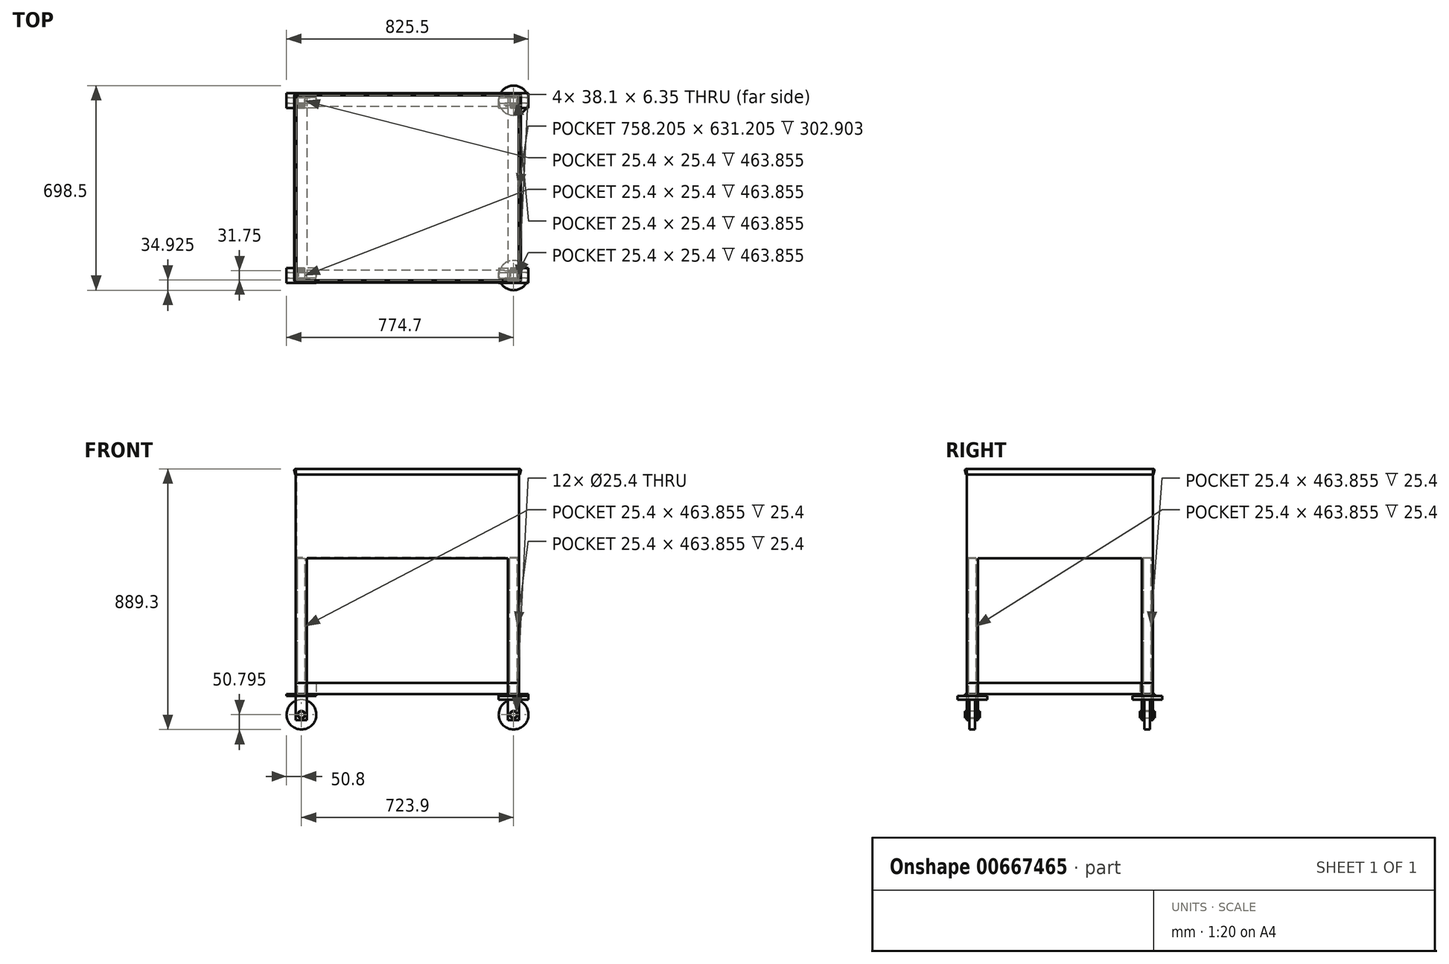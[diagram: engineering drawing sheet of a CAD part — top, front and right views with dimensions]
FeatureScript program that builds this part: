
annotation { "Feature Type Name" : "Feature", "Feature Type Description" : "" }
export const myFeature = defineFeature(function(context is Context, id is Id, definition is map)
    precondition{}
    {
        {
            var Q0;
            Q0=qCreatedBy(makeId("Top.planeOp"),FACE);
            var sketch = newSketch(context, id + "F0", { "sketchPlane" : qUnion([Q0])});
            skLineSegment(sketch, "E0.bottom", {"start": v(381, -317.5) * mm, "end": v(-381, -317.5) * mm});
            skLineSegment(sketch, "E0.top", {"start": v(381, 317.5) * mm, "end": v(-381, 317.5) * mm});
            skLineSegment(sketch, "E0.left", {"start": v(381, -317.5) * mm, "end": v(381, 317.5) * mm});
            skLineSegment(sketch, "E0.right", {"start": v(-381, -317.5) * mm, "end": v(-381, 317.5) * mm});
            skPoint(sketch, "E0.middle", {"position": v(0, 0) * mm});
            skSolve(sketch);
        }
        {
            var Q0;
            Q0=makeQuery(id+"F0.imprint","IMPRINT",FACE,{"disambiguationData":[TD([[makeQuery(id+"F0.imprint","IMPRINT",EDGE,{"derivedFrom":sQuery(id+"F0.wireOp",EDGE,"E0.bottom")}),-1.0]])]});
            extrude(context, id + "F1", {"entities" : qUnion([Q0]), "depth" : 304.8 * mm, "offsetDistance" : 25.4 * mm});
        }
        {
            var Q0;
            Q0=makeQuery(id+"F1.opExtrude","CAP_FACE",FACE,{"disambiguationData":[OSD([sQuery(id+"F0.wireOp",EDGE,"E0.bottom"),sQuery(id+"F0.wireOp",EDGE,"E0.top"),sQuery(id+"F0.wireOp",EDGE,"E0.left"),sQuery(id+"F0.wireOp",EDGE,"E0.right")])],"isStart":false});
            shell(context, id + "F2", {"entities" : qUnion([Q0]), "thickness" : 1.9 * mm});
        }
        {
            var Q0;
            Q0=makeQuery(id+"F1.opExtrude","CAP_FACE",FACE,{"disambiguationData":[OSD([sQuery(id+"F0.wireOp",EDGE,"E0.bottom"),sQuery(id+"F0.wireOp",EDGE,"E0.top"),sQuery(id+"F0.wireOp",EDGE,"E0.left"),sQuery(id+"F0.wireOp",EDGE,"E0.right")])],"isStart":true});
            var sketch = newSketch(context, id + "F3", { "sketchPlane" : qUnion([Q0])});
            skLineSegment(sketch, "E1.bottom", {"start": v(-381, 317.5) * mm, "end": v(-342.9, 317.5) * mm});
            skLineSegment(sketch, "E1.top", {"start": v(-381, 279.4) * mm, "end": v(-342.9, 279.4) * mm});
            skLineSegment(sketch, "E1.left", {"start": v(-381, 317.5) * mm, "end": v(-381, 279.4) * mm});
            skLineSegment(sketch, "E1.right", {"start": v(-342.9, 317.5) * mm, "end": v(-342.9, 279.4) * mm});
            skLineSegment(sketch, "E2.0", {"start": v(-374.65, 285.75) * mm, "end": v(-349.25, 285.75) * mm});
            skLineSegment(sketch, "E2.1", {"start": v(-374.65, 311.15) * mm, "end": v(-374.65, 285.75) * mm});
            skLineSegment(sketch, "E2.2", {"start": v(-374.65, 311.15) * mm, "end": v(-349.25, 311.15) * mm});
            skLineSegment(sketch, "E2.3", {"start": v(-349.25, 311.15) * mm, "end": v(-349.25, 285.75) * mm});
            skSolve(sketch);
        }
        {
            var Q0;
            Q0=makeQuery(id+"F3.imprint","IMPRINT",FACE,{"disambiguationData":[TD([[makeQuery(id+"F3.imprint","IMPRINT",EDGE,{"derivedFrom":sQuery(id+"F3.wireOp",EDGE,"E1.bottom")}),1.0]])]});
            extrude(context, id + "F4", {"entities" : qUnion([Q0]), "depth" : 457.2 * mm + 6.65 * mm, "offsetDistance" : 25.4 * mm});
        }
        {
            var Q0;
            Q0=makeQuery(id+"F4.opExtrude","CAP_FACE",FACE,{"disambiguationData":[OSD([sQuery(id+"F3.wireOp",EDGE,"E1.bottom"),sQuery(id+"F3.wireOp",EDGE,"E1.top"),sQuery(id+"F3.wireOp",EDGE,"E1.left"),sQuery(id+"F3.wireOp",EDGE,"E1.right"),sQuery(id+"F3.wireOp",EDGE,"E2.0"),sQuery(id+"F3.wireOp",EDGE,"E2.1"),sQuery(id+"F3.wireOp",EDGE,"E2.2"),sQuery(id+"F3.wireOp",EDGE,"E2.3")])],"isStart":false});
            var sketch = newSketch(context, id + "F5", { "sketchPlane" : qUnion([Q0])});
            skLineSegment(sketch, "E3.bottom", {"start": v(-311.15, 273.05) * mm, "end": v(-412.75, 273.05) * mm});
            skLineSegment(sketch, "E3.top", {"start": v(-311.15, 323.85) * mm, "end": v(-412.75, 323.85) * mm});
            skLineSegment(sketch, "E3.left", {"start": v(-311.15, 273.05) * mm, "end": v(-311.15, 323.85) * mm});
            skLineSegment(sketch, "E3.right", {"start": v(-412.75, 273.05) * mm, "end": v(-412.75, 323.85) * mm});
            skPoint(sketch, "E3.middle", {"position": v(-361.95, 298.45) * mm});
            skPoint(sketch, "E3.middle.positionSnap0", {"position": v(-374.65, 298.45) * mm});
            skPoint(sketch, "E3.middle.positionSnap1", {"position": v(-361.95, 311.15) * mm});
            skPoint(sketch, "E3.centerSnap0", {"position": v(-374.65, 298.45) * mm});
            skPoint(sketch, "E3.centerSnap1", {"position": v(-361.95, 311.15) * mm});
            skSolve(sketch);
        }
        {
            var Q0;
            Q0=makeQuery(id+"F5.imprint","IMPRINT",FACE,{"disambiguationData":[TD([[makeQuery(id+"F5.imprint","IMPRINT",EDGE,{"derivedFrom":sQuery(id+"F5.wireOp",EDGE,"E3.bottom")}),-1.0]])]});
            var Q1;
            Q1=makeQuery(id+"F5.imprint","IMPRINT",FACE,{"disambiguationData":[TD([[makeQuery(id+"F5.imprint","IMPRINT",EDGE,{"derivedFrom":makeQuery(id+"F4.opExtrude","CAP_EDGE",EDGE,{"disambiguationData":[OSD([sQuery(id+"F3.wireOp",EDGE,"E1.bottom")])],"isStart":false})}),1.0]])]});
            var Q2;
            Q2=makeQuery(id+"F5.imprint","IMPRINT",FACE,{"disambiguationData":[TD([[makeQuery(id+"F5.imprint","IMPRINT",EDGE,{"derivedFrom":makeQuery(id+"F4.opExtrude","CAP_EDGE",EDGE,{"disambiguationData":[OSD([sQuery(id+"F3.wireOp",EDGE,"E2.0")])],"isStart":false})}),1.0]])]});
            extrude(context, id + "F6", {"entities" : qUnion([Q0, Q1, Q2]), "depth" : 6.35 * mm, "offsetDistance" : 25.4 * mm});
        }
        {
            var Q0;
            Q0=makeQuery(id+"F4.opExtrude","SWEPT_FACE",FACE,{"disambiguationData":[OSD([sQuery(id+"F3.wireOp",EDGE,"E1.bottom")])]});
            var sketch = newSketch(context, id + "F7", { "sketchPlane" : qUnion([Q0])});
            skLineSegment(sketch, "E4", {"start": v(-381, -463.85) * mm, "end": v(-381, -552.75) * mm});
            skLineSegment(sketch, "E5", {"start": v(-381, -552.75) * mm, "end": v(-342.9, -552.75) * mm});
            skLineSegment(sketch, "E6", {"start": v(-342.9, -552.75) * mm, "end": v(-342.9, -463.85) * mm});
            skCircle(sketch, "E7", {"center": v(-361.95, -533.7) * mm, "radius": 12.7 * mm});
            skSolve(sketch);
        }
        {
            var Q0;
            Q0=makeQuery(id+"F7.imprint","IMPRINT",FACE,{"disambiguationData":[TD([[makeQuery(id+"F7.imprint","IMPRINT",EDGE,{"derivedFrom":sQuery(id+"F7.wireOp",EDGE,"E4")}),1.0]])]});
            extrude(context, id + "F8", {"entities" : qUnion([Q0]), "depth" : -6.35 * mm, "offsetDistance" : 25.4 * mm});
        }
        {
            var Q0;
            Q0=makeQuery(id+"F6.opExtrude","SWEPT_FACE",FACE,{"disambiguationData":[OSD([sQuery(id+"F5.wireOp",EDGE,"E3.bottom")])]});
            var Q1;
            Q1=makeQuery(id+"F6.opExtrude","SWEPT_FACE",FACE,{"disambiguationData":[OSD([sQuery(id+"F5.wireOp",EDGE,"E3.top")])]});
            cPlane(context, id + "F9", {"entities" : qUnion([Q0, Q1]), "cplaneType" : CPlaneType.MID_PLANE, "offset" : 25.4 * mm, "width" : 152.4 * mm, "height" : 152.4 * mm});
        }
        {
            var Q0;
            Q0=makeQuery(id+"F8.opExtrude","SWEPT_BODY",BODY,{"disambiguationData":[OSD([sQuery(id+"F3.wireOp",EDGE,"E1.bottom"),sQuery(id+"F7.wireOp",EDGE,"E4"),sQuery(id+"F7.wireOp",EDGE,"E5"),sQuery(id+"F7.wireOp",EDGE,"E6"),sQuery(id+"F7.wireOp",EDGE,"E7")])]});
            var Q1;
            Q1=qCreatedBy(id+"F9.planeOp",FACE);
            mirror(context, id + "F10", {"operationType" : NewBodyOperationType.ADD, "entities" : qUnion([Q0]), "mirrorPlane" : qUnion([Q1])});
        }
        {
            var Q0;
            Q0=qCreatedBy(id+"F9.planeOp",FACE);
            var sketch = newSketch(context, id + "F11", { "sketchPlane" : qUnion([Q0])});
            skCircle(sketch, "E8", {"center": v(361.95, -533.7) * mm, "radius": 50.8 * mm});
            skCircle(sketch, "E9", {"center": v(361.95, -533.7) * mm, "radius": 12.7 * mm});
            skSolve(sketch);
        }
        {
            var Q0;
            Q0=makeQuery(id+"F11.imprint","IMPRINT",FACE,{"disambiguationData":[TD([[makeQuery(id+"F11.imprint","IMPRINT",EDGE,{"derivedFrom":sQuery(id+"F11.wireOp",EDGE,"E8")}),1.0]])]});
            extrude(context, id + "F12", {"entities" : qUnion([Q0]), "oppositeDirection" : true, "depth" : 19.05 * mm, "offsetDistance" : 25.4 * mm, "symmetric" : true});
        }
        {
            var Q0;
            Q0=qCreatedBy(id+"F9.planeOp",FACE);
            var sketch = newSketch(context, id + "F13", { "sketchPlane" : qUnion([Q0])});
            skCircle(sketch, "E10", {"center": v(361.95, -533.7) * mm, "radius": 11.11 * mm});
            skSolve(sketch);
        }
        {
            var Q0;
            Q0=makeQuery(id+"F13.imprint","IMPRINT",FACE,{"disambiguationData":[TD([[makeQuery(id+"F13.imprint","IMPRINT",EDGE,{"derivedFrom":sQuery(id+"F13.wireOp",EDGE,"E10")}),1.0]])]});
            extrude(context, id + "F14", {"entities" : qUnion([Q0]), "depth" : 50.8 * mm, "offsetDistance" : 25.4 * mm, "symmetric" : true});
        }
        {
            var Q0;
            Q0=makeQuery(id+"F12.opExtrude","SWEPT_BODY",BODY,{"disambiguationData":[OSD([sQuery(id+"F11.wireOp",EDGE,"E8"),sQuery(id+"F11.wireOp",EDGE,"E9")])]});
            var Q1;
            Q1=makeQuery(id+"F10.opPattern","COPY",BODY,{"derivedFrom":makeQuery(id+"F8.opExtrude","SWEPT_BODY",BODY,{"disambiguationData":[OSD([sQuery(id+"F3.wireOp",EDGE,"E1.bottom"),sQuery(id+"F7.wireOp",EDGE,"E4"),sQuery(id+"F7.wireOp",EDGE,"E5"),sQuery(id+"F7.wireOp",EDGE,"E6"),sQuery(id+"F7.wireOp",EDGE,"E7")])]}),"instanceName":"1"});
            var Q2;
            Q2=makeQuery(id+"F8.opExtrude","SWEPT_BODY",BODY,{"disambiguationData":[OSD([sQuery(id+"F3.wireOp",EDGE,"E1.bottom"),sQuery(id+"F7.wireOp",EDGE,"E4"),sQuery(id+"F7.wireOp",EDGE,"E5"),sQuery(id+"F7.wireOp",EDGE,"E6"),sQuery(id+"F7.wireOp",EDGE,"E7")])]});
            var Q3;
            Q3=makeQuery(id+"F4.opExtrude","SWEPT_BODY",BODY,{"disambiguationData":[OSD([sQuery(id+"F3.wireOp",EDGE,"E1.bottom"),sQuery(id+"F3.wireOp",EDGE,"E1.top"),sQuery(id+"F3.wireOp",EDGE,"E1.left"),sQuery(id+"F3.wireOp",EDGE,"E1.right"),sQuery(id+"F3.wireOp",EDGE,"E2.0"),sQuery(id+"F3.wireOp",EDGE,"E2.1"),sQuery(id+"F3.wireOp",EDGE,"E2.2"),sQuery(id+"F3.wireOp",EDGE,"E2.3")])]});
            var Q4;
            Q4=makeQuery(id+"F6.opExtrude","SWEPT_BODY",BODY,{"disambiguationData":[OSD([sQuery(id+"F5.wireOp",EDGE,"E3.bottom"),sQuery(id+"F5.wireOp",EDGE,"E3.top"),sQuery(id+"F5.wireOp",EDGE,"E3.left"),sQuery(id+"F5.wireOp",EDGE,"E3.right")])]});
            var Q5;
            Q5=makeQuery(id+"F14.opExtrude","SWEPT_BODY",BODY,{"disambiguationData":[OSD([sQuery(id+"F13.wireOp",EDGE,"E10")])]});
            var Q6;
            Q6=qCreatedBy(makeId("Front.planeOp"),FACE);
            mirror(context, id + "F15", {"operationType" : NewBodyOperationType.ADD, "entities" : qUnion([Q0, Q1, Q2, Q3, Q4, Q5]), "mirrorPlane" : qUnion([Q6])});
        }
        {
            var Q0;
            Q0=makeQuery(id+"F12.opExtrude","SWEPT_BODY",BODY,{"disambiguationData":[OSD([sQuery(id+"F11.wireOp",EDGE,"E8"),sQuery(id+"F11.wireOp",EDGE,"E9")])]});
            var Q1;
            Q1=makeQuery(id+"F1.opExtrude","SWEPT_BODY",BODY,{"disambiguationData":[OSD([sQuery(id+"F0.wireOp",EDGE,"E0.bottom"),sQuery(id+"F0.wireOp",EDGE,"E0.top"),sQuery(id+"F0.wireOp",EDGE,"E0.left"),sQuery(id+"F0.wireOp",EDGE,"E0.right")])]});
            var Q2;
            Q2=makeQuery(id+"F14.opExtrude","SWEPT_BODY",BODY,{"disambiguationData":[OSD([sQuery(id+"F13.wireOp",EDGE,"E10")])]});
            var Q3;
            Q3=makeQuery(id+"F15.opPattern","COPY",BODY,{"derivedFrom":makeQuery(id+"F12.opExtrude","SWEPT_BODY",BODY,{"disambiguationData":[OSD([sQuery(id+"F11.wireOp",EDGE,"E8"),sQuery(id+"F11.wireOp",EDGE,"E9")])]}),"instanceName":"1"});
            var Q4;
            Q4=makeQuery(id+"F15.opPattern","COPY",BODY,{"derivedFrom":makeQuery(id+"F14.opExtrude","SWEPT_BODY",BODY,{"disambiguationData":[OSD([sQuery(id+"F13.wireOp",EDGE,"E10")])]}),"instanceName":"1"});
            var Q5;
            Q5=qCreatedBy(makeId("Right.planeOp"),FACE);
            mirror(context, id + "F16", {"operationType" : NewBodyOperationType.ADD, "entities" : qUnion([Q0, Q1, Q2, Q3, Q4]), "mirrorPlane" : qUnion([Q5])});
        }
        {
            var Q0;
            Q0=makeQuery(id+"F16.opPattern","COPY",FACE,{"derivedFrom":makeQuery(id+"F15.opPattern","COPY",FACE,{"derivedFrom":makeQuery(id+"F6.opExtrude","CAP_FACE",FACE,{"disambiguationData":[OSD([sQuery(id+"F5.wireOp",EDGE,"E3.bottom"),sQuery(id+"F5.wireOp",EDGE,"E3.top"),sQuery(id+"F5.wireOp",EDGE,"E3.left"),sQuery(id+"F5.wireOp",EDGE,"E3.right")])],"isStart":false}),"instanceName":"1"}),"instanceName":"1"});
            var sketch = newSketch(context, id + "F17", { "sketchPlane" : qUnion([Q0])});
            skCircle(sketch, "E11", {"center": v(361.95, -298.45) * mm, "radius": 50.8 * mm});
            skPoint(sketch, "E11.centerSnap0", {"position": v(412.75, -298.45) * mm});
            skLineSegment(sketch, "E12", {"start": v(361.95, -273.05) * mm, "end": v(361.95, -323.85) * mm});
            skSolve(sketch);
        }
        {
            var Q0;
            {var subQ0=sQuery(id+"F17.wireOp",EDGE,"E11");var subQ1=makeQuery(id+"F16.opPattern","COPY",EDGE,{"derivedFrom":makeQuery(id+"F15.opPattern","COPY",EDGE,{"derivedFrom":makeQuery(id+"F6.opExtrude","CAP_EDGE",EDGE,{"disambiguationData":[OSD([sQuery(id+"F5.wireOp",EDGE,"E3.bottom")])],"isStart":false}),"instanceName":"1"}),"instanceName":"1"});var subQ2=makeQuery(id+"F17.imprint","INTERSECT",VERTEX,{"disambiguationData":[OD(0.0)],"derivedFrom":[subQ1,subQ0]});Q0=makeQuery(id+"F17.imprint","IMPRINT",FACE,{"disambiguationData":[TD([[makeQuery(id+"F17.imprint","IMPRINT",EDGE,{"disambiguationData":[TD([[subQ2,1.0]])],"derivedFrom":subQ0}),1.0]])]});}
            var Q1;
            {var subQ7=sQuery(id+"F5.wireOp",EDGE,"E3.bottom");var subQ20=sQuery(id+"F17.wireOp",EDGE,"E11");var subQ21=makeQuery(id+"F16.opPattern","COPY",EDGE,{"derivedFrom":makeQuery(id+"F15.opPattern","COPY",EDGE,{"derivedFrom":makeQuery(id+"F6.opExtrude","CAP_EDGE",EDGE,{"disambiguationData":[OSD([subQ7])],"isStart":false}),"instanceName":"1"}),"instanceName":"1"});var subQ22=makeQuery(id+"F17.imprint","INTERSECT",VERTEX,{"disambiguationData":[OD(1.0)],"derivedFrom":[subQ21,subQ20]});Q1=makeQuery(id+"F17.imprint","IMPRINT",FACE,{"disambiguationData":[TD([[makeQuery(id+"F17.imprint","IMPRINT",EDGE,{"disambiguationData":[TD([[subQ22,1.0]])],"derivedFrom":subQ20}),1.0]])]});}
            var Q2;
            {var subQ3=sQuery(id+"F5.wireOp",EDGE,"E3.bottom");var subQ14=sQuery(id+"F17.wireOp",EDGE,"E11");var subQ15=makeQuery(id+"F16.opPattern","COPY",EDGE,{"derivedFrom":makeQuery(id+"F15.opPattern","COPY",EDGE,{"derivedFrom":makeQuery(id+"F6.opExtrude","CAP_EDGE",EDGE,{"disambiguationData":[OSD([subQ3])],"isStart":false}),"instanceName":"1"}),"instanceName":"1"});var subQ16=makeQuery(id+"F17.imprint","INTERSECT",VERTEX,{"disambiguationData":[OD(0.0)],"derivedFrom":[subQ15,subQ14]});Q2=makeQuery(id+"F17.imprint","IMPRINT",FACE,{"disambiguationData":[TD([[makeQuery(id+"F17.imprint","IMPRINT",EDGE,{"disambiguationData":[TD([[subQ16,-1.0]])],"derivedFrom":subQ14}),1.0]])]});}
            var Q3;
            {var subQ0=sQuery(id+"F17.wireOp",EDGE,"E11");var subQ1=makeQuery(id+"F16.opPattern","COPY",EDGE,{"derivedFrom":makeQuery(id+"F15.opPattern","COPY",EDGE,{"derivedFrom":makeQuery(id+"F6.opExtrude","CAP_EDGE",EDGE,{"disambiguationData":[OSD([sQuery(id+"F5.wireOp",EDGE,"E3.top")])],"isStart":false}),"instanceName":"1"}),"instanceName":"1"});var subQ2=makeQuery(id+"F17.imprint","INTERSECT",VERTEX,{"disambiguationData":[OD(0.0)],"derivedFrom":[subQ1,subQ0]});Q3=makeQuery(id+"F17.imprint","IMPRINT",FACE,{"disambiguationData":[TD([[makeQuery(id+"F17.imprint","IMPRINT",EDGE,{"disambiguationData":[TD([[subQ2,-1.0]])],"derivedFrom":subQ0}),1.0]])]});}
            var Q4;
            {var subQ4=sQuery(id+"F5.wireOp",EDGE,"E3.bottom");var subQ15=sQuery(id+"F17.wireOp",EDGE,"E11");var subQ23=makeQuery(id+"F16.opPattern","COPY",EDGE,{"derivedFrom":makeQuery(id+"F15.opPattern","COPY",EDGE,{"derivedFrom":makeQuery(id+"F6.opExtrude","CAP_EDGE",EDGE,{"disambiguationData":[OSD([subQ4])],"isStart":false}),"instanceName":"1"}),"instanceName":"1"});var subQ24=makeQuery(id+"F17.imprint","INTERSECT",VERTEX,{"disambiguationData":[OD(1.0)],"derivedFrom":[subQ23,subQ15]});Q4=makeQuery(id+"F17.imprint","IMPRINT",FACE,{"disambiguationData":[TD([[makeQuery(id+"F17.imprint","IMPRINT",EDGE,{"disambiguationData":[TD([[subQ24,-1.0]])],"derivedFrom":subQ15}),1.0]])]});}
            var Q5;
            Q5=sQuery(id+"F17.wireOp",EDGE,"E11");
            extrude(context, id + "F18", {"entities" : qUnion([Q0, Q1, Q2, Q3, Q4]), "surfaceEntities" : qUnion([Q5]), "depth" : 12.7 * mm, "offsetDistance" : 25.4 * mm});
        }
        {
            var Q0;
            Q0=makeQuery(id+"F18.opExtrude","SWEPT_BODY",BODY,{"disambiguationData":[OSD([sQuery(id+"F3.wireOp",EDGE,"E1.bottom"),sQuery(id+"F5.wireOp",EDGE,"E3.bottom"),sQuery(id+"F5.wireOp",EDGE,"E3.top"),sQuery(id+"F5.wireOp",EDGE,"E3.left"),sQuery(id+"F5.wireOp",EDGE,"E3.right"),sQuery(id+"F7.wireOp",EDGE,"E4"),sQuery(id+"F7.wireOp",EDGE,"E5"),sQuery(id+"F7.wireOp",EDGE,"E6"),sQuery(id+"F7.wireOp",EDGE,"E7"),sQuery(id+"F17.wireOp",EDGE,"E11")])]});
            var Q1;
            Q1=qCreatedBy(makeId("Front.planeOp"),FACE);
            mirror(context, id + "F19", {"entities" : qUnion([Q0]), "mirrorPlane" : qUnion([Q1])});
        }
        {
            var Q0;
            {var subQ0=makeQuery(id+"F4.opExtrude","SWEPT_FACE",FACE,{"disambiguationData":[OSD([sQuery(id+"F3.wireOp",EDGE,"E1.left")])]});Q0=makeQuery(id+"F15.boolean.opBoolean","MERGE",FACE,{"derivedFrom":[makeQuery(id+"F1.opExtrude","SWEPT_FACE",FACE,{"disambiguationData":[OSD([sQuery(id+"F0.wireOp",EDGE,"E0.right")])]}),subQ0,makeQuery(id+"F15.opPattern","COPY",FACE,{"derivedFrom":subQ0,"instanceName":"1"})]});}
            var sketch = newSketch(context, id + "F20", { "sketchPlane" : qUnion([Q0])});
            skLineSegment(sketch, "E13", {"start": v(-317.5, 304.8) * mm, "end": v(-319.05, 304.8) * mm});
            skLineSegment(sketch, "E14", {"start": v(-322.75, 300.13) * mm, "end": v(-319.35, 285.75) * mm});
            skLineSegment(sketch, "E15.0", {"start": v(-320.9, 300.57) * mm, "end": v(-317.5, 286.19) * mm});
            skLineSegment(sketch, "E15.1", {"start": v(-317.5, 302.9) * mm, "end": v(-319.05, 302.9) * mm});
            skLineSegment(sketch, "E16", {"start": v(-317.5, 286.19) * mm, "end": v(-319.35, 285.75) * mm});
            skPoint(sketch, "E17.visualSharp", {"position": v(-323.85, 304.8) * mm});
            skArc(sketch, "E17.filletArc", {"start": v(-319.05, 304.8) * mm, "mid": v(-322.03, 303.36) * mm, "end": v(-322.75, 300.13) * mm});
            skPoint(sketch, "E18.visualSharp", {"position": v(-321.45, 302.9) * mm});
            skArc(sketch, "E18.filletArc", {"start": v(-319.05, 302.9) * mm, "mid": v(-320.54, 302.18) * mm, "end": v(-320.9, 300.57) * mm});
            skLineSegment(sketch, "E19.MirrorCS", {"start": v(317.5, 302.9) * mm, "end": v(319.05, 302.9) * mm});
            skLineSegment(sketch, "E20.MirrorCS", {"start": v(317.5, 304.8) * mm, "end": v(319.05, 304.8) * mm});
            skArc(sketch, "E21.MirrorCS", {"start": v(319.05, 304.8) * mm, "mid": v(322.03, 303.36) * mm, "end": v(322.75, 300.13) * mm});
            skLineSegment(sketch, "E22.MirrorCS", {"start": v(322.75, 300.13) * mm, "end": v(319.35, 285.75) * mm});
            skPoint(sketch, "E23.MirrorP", {"position": v(323.85, 304.8) * mm});
            skLineSegment(sketch, "E24.MirrorCS", {"start": v(320.9, 300.57) * mm, "end": v(317.5, 286.19) * mm});
            skLineSegment(sketch, "E25.MirrorCS", {"start": v(317.5, 286.19) * mm, "end": v(319.35, 285.75) * mm});
            skArc(sketch, "E26.MirrorCS", {"start": v(319.05, 302.9) * mm, "mid": v(320.54, 302.18) * mm, "end": v(320.9, 300.57) * mm});
            skPoint(sketch, "E27.MirrorP", {"position": v(321.45, 302.9) * mm});
            skSolve(sketch);
        }
        {
            var Q0;
            {var subQ1=sQuery(id+"F20.wireOp",EDGE,"E13");Q0=makeQuery(id+"F20.imprint","IMPRINT",FACE,{"disambiguationData":[TD([[makeQuery(id+"F20.imprint","IMPRINT",EDGE,{"derivedFrom":subQ1}),1.0]])]});}
            var Q1;
            {var subQ3=sQuery(id+"F20.wireOp",EDGE,"E19.MirrorCS");Q1=makeQuery(id+"F20.imprint","IMPRINT",FACE,{"disambiguationData":[TD([[makeQuery(id+"F20.imprint","IMPRINT",EDGE,{"derivedFrom":subQ3}),1.0]])]});}
            var Q2;
            {var subQ0=makeQuery(id+"F4.opExtrude","SWEPT_FACE",FACE,{"disambiguationData":[OSD([sQuery(id+"F3.wireOp",EDGE,"E1.left")])]});Q2=makeQuery(id+"F16.boolean.opBoolean","MERGE",FACE,{"derivedFrom":[makeQuery(id+"F1.opExtrude","SWEPT_FACE",FACE,{"disambiguationData":[OSD([sQuery(id+"F0.wireOp",EDGE,"E0.left")])]}),makeQuery(id+"F16.opPattern","COPY",FACE,{"derivedFrom":makeQuery(id+"F15.boolean.opBoolean","MERGE",FACE,{"derivedFrom":[makeQuery(id+"F1.opExtrude","SWEPT_FACE",FACE,{"disambiguationData":[OSD([sQuery(id+"F0.wireOp",EDGE,"E0.right")])]}),subQ0,makeQuery(id+"F15.opPattern","COPY",FACE,{"derivedFrom":subQ0,"instanceName":"1"})]}),"instanceName":"1"})]});}
            var Q3;
            Q3=makeQuery(id+"F1.opExtrude","SWEPT_BODY",BODY,{"disambiguationData":[OSD([sQuery(id+"F0.wireOp",EDGE,"E0.bottom"),sQuery(id+"F0.wireOp",EDGE,"E0.top"),sQuery(id+"F0.wireOp",EDGE,"E0.left"),sQuery(id+"F0.wireOp",EDGE,"E0.right")])]});
            var Q4;
            {var subQ0=makeQuery(id+"F4.opExtrude","SWEPT_FACE",FACE,{"disambiguationData":[OSD([sQuery(id+"F3.wireOp",EDGE,"E1.left")])]});Q4=makeQuery(id+"F15.boolean.opBoolean","MERGE",FACE,{"derivedFrom":[makeQuery(id+"F1.opExtrude","SWEPT_FACE",FACE,{"disambiguationData":[OSD([sQuery(id+"F0.wireOp",EDGE,"E0.right")])]}),subQ0,makeQuery(id+"F15.opPattern","COPY",FACE,{"derivedFrom":subQ0,"instanceName":"1"})]});}
            extrude(context, id + "F21", {"entities" : qUnion([Q0, Q1]), "endBound" : BoundingType.UP_TO_SURFACE, "oppositeDirection" : true, "depth" : 25.4 * mm, "endBoundEntityFace" : qUnion([Q2]), "endBoundEntityBody" : qUnion([Q3]), "offsetDistance" : 0 * mm});
        }
        {
            var Q0;
            {var subQ0=makeQuery(id+"F15.boolean.opBoolean","MERGE",FACE,{"derivedFrom":[makeQuery(id+"F1.opExtrude","SWEPT_FACE",FACE,{"disambiguationData":[OSD([sQuery(id+"F0.wireOp",EDGE,"E0.top")])]}),makeQuery(id+"F15.opPattern","COPY",FACE,{"derivedFrom":makeQuery(id+"F4.opExtrude","SWEPT_FACE",FACE,{"disambiguationData":[OSD([sQuery(id+"F3.wireOp",EDGE,"E1.bottom")])]}),"instanceName":"1"})]});Q0=makeQuery(id+"F16.boolean.opBoolean","MERGE",FACE,{"derivedFrom":[subQ0,makeQuery(id+"F16.opPattern","COPY",FACE,{"derivedFrom":subQ0,"instanceName":"1"})]});}
            var sketch = newSketch(context, id + "F22", { "sketchPlane" : qUnion([Q0])});
            skLineSegment(sketch, "E28", {"start": v(-381, 304.8) * mm, "end": v(-383.15, 304.5) * mm});
            skLineSegment(sketch, "E29", {"start": v(-386.32, 299.86) * mm, "end": v(-382.85, 285.3) * mm});
            skLineSegment(sketch, "E30.0", {"start": v(-384.47, 300.3) * mm, "end": v(-381, 285.75) * mm});
            skLineSegment(sketch, "E30.1", {"start": v(-381, 302.88) * mm, "end": v(-382.89, 302.62) * mm});
            skLineSegment(sketch, "E31", {"start": v(-381, 285.75) * mm, "end": v(-382.85, 285.3) * mm});
            skPoint(sketch, "E32.visualSharp", {"position": v(-387.29, 303.92) * mm});
            skArc(sketch, "E32.filletArc", {"start": v(-383.15, 304.5) * mm, "mid": v(-385.76, 302.88) * mm, "end": v(-386.32, 299.86) * mm});
            skPoint(sketch, "E33.visualSharp", {"position": v(-384.96, 302.33) * mm});
            skArc(sketch, "E33.filletArc", {"start": v(-382.89, 302.62) * mm, "mid": v(-384.2, 301.81) * mm, "end": v(-384.47, 300.3) * mm});
            skLineSegment(sketch, "E34.MirrorCS", {"start": v(381, 304.8) * mm, "end": v(383.15, 304.5) * mm});
            skLineSegment(sketch, "E35.MirrorCS", {"start": v(381, 302.88) * mm, "end": v(382.89, 302.62) * mm});
            skArc(sketch, "E36.MirrorCS", {"start": v(382.89, 302.62) * mm, "mid": v(384.2, 301.81) * mm, "end": v(384.47, 300.3) * mm});
            skLineSegment(sketch, "E37.MirrorCS", {"start": v(381, 285.75) * mm, "end": v(382.85, 285.3) * mm});
            skArc(sketch, "E38.MirrorCS", {"start": v(383.15, 304.5) * mm, "mid": v(385.76, 302.88) * mm, "end": v(386.32, 299.86) * mm});
            skPoint(sketch, "E39.MirrorP", {"position": v(384.96, 302.33) * mm});
            skPoint(sketch, "E40.MirrorP", {"position": v(387.29, 303.92) * mm});
            skLineSegment(sketch, "E41.MirrorCS", {"start": v(384.47, 300.3) * mm, "end": v(381, 285.75) * mm});
            skLineSegment(sketch, "E42.MirrorCS", {"start": v(386.32, 299.86) * mm, "end": v(382.85, 285.3) * mm});
            skSolve(sketch);
        }
        {
            var Q0;
            {var subQ1=sQuery(id+"F22.wireOp",EDGE,"E28");Q0=makeQuery(id+"F22.imprint","IMPRINT",FACE,{"disambiguationData":[TD([[makeQuery(id+"F22.imprint","IMPRINT",EDGE,{"derivedFrom":subQ1}),1.0]])]});}
            var Q1;
            {var subQ1=sQuery(id+"F22.wireOp",EDGE,"E34.MirrorCS");Q1=makeQuery(id+"F22.imprint","IMPRINT",FACE,{"disambiguationData":[TD([[makeQuery(id+"F22.imprint","IMPRINT",EDGE,{"derivedFrom":subQ1}),-1.0]])]});}
            var Q2;
            {var subQ0=makeQuery(id+"F15.boolean.opBoolean","MERGE",FACE,{"derivedFrom":[makeQuery(id+"F1.opExtrude","SWEPT_FACE",FACE,{"disambiguationData":[OSD([sQuery(id+"F0.wireOp",EDGE,"E0.bottom")])]}),makeQuery(id+"F4.opExtrude","SWEPT_FACE",FACE,{"disambiguationData":[OSD([sQuery(id+"F3.wireOp",EDGE,"E1.bottom")])]})]});Q2=makeQuery(id+"F16.boolean.opBoolean","MERGE",FACE,{"derivedFrom":[subQ0,makeQuery(id+"F16.opPattern","COPY",FACE,{"derivedFrom":subQ0,"instanceName":"1"})]});}
            extrude(context, id + "F23", {"entities" : qUnion([Q0, Q1]), "endBound" : BoundingType.UP_TO_SURFACE, "oppositeDirection" : true, "depth" : 25.4 * mm, "endBoundEntityFace" : qUnion([Q2]), "offsetDistance" : 25.4 * mm});
        }
        {
            var Q0;
            {var subQ0=sQuery(id+"F5.wireOp",EDGE,"E3.bottom");var subQ2=sQuery(id+"F5.wireOp",EDGE,"E3.left");var subQ3=sQuery(id+"F5.wireOp",EDGE,"E3.top");var subQ4=sQuery(id+"F5.wireOp",EDGE,"E3.right");Q0=makeQuery(id+"F15.boolean.opBoolean","SPLIT",FACE,{"disambiguationData":[TD([makeQuery(id+"F1.opExtrude","SWEPT_FACE",FACE,{"disambiguationData":[OSD([sQuery(id+"F0.wireOp",EDGE,"E0.top")])]})])],"derivedFrom":makeQuery(id+"F15.opPattern","COPY",FACE,{"derivedFrom":makeQuery(id+"F6.opExtrude","CAP_FACE",FACE,{"disambiguationData":[OSD([subQ0,subQ3,subQ2,subQ4])],"isStart":true}),"instanceName":"1"})});}
            var sketch = newSketch(context, id + "F24", { "sketchPlane" : qUnion([Q0])});
            skLineSegment(sketch, "E43.bottom", {"start": v(-381, 317.5) * mm, "end": v(381, 317.5) * mm});
            skLineSegment(sketch, "E43.top", {"start": v(-381, -317.5) * mm, "end": v(381, -317.5) * mm});
            skLineSegment(sketch, "E43.left", {"start": v(-381, 317.5) * mm, "end": v(-381, -317.5) * mm});
            skLineSegment(sketch, "E43.right", {"start": v(381, 317.5) * mm, "end": v(381, -317.5) * mm});
            skLineSegment(sketch, "E44.bottom", {"start": v(-342.9, 279.4) * mm, "end": v(342.9, 279.4) * mm});
            skLineSegment(sketch, "E44.top", {"start": v(-342.9, -279.4) * mm, "end": v(342.9, -279.4) * mm});
            skLineSegment(sketch, "E44.left", {"start": v(-342.9, 279.4) * mm, "end": v(-342.9, -279.4) * mm});
            skLineSegment(sketch, "E44.right", {"start": v(342.9, 279.4) * mm, "end": v(342.9, -279.4) * mm});
            skSolve(sketch);
        }
        {
            var Q0;
            {var subQ2=sQuery(id+"F24.wireOp",EDGE,"E43.top");Q0=makeQuery(id+"F24.imprint","IMPRINT",FACE,{"disambiguationData":[TD([[makeQuery(id+"F24.imprint","IMPRINT",EDGE,{"derivedFrom":subQ2}),1.0]])]});}
            var Q1;
            {var subQ1=makeQuery(id+"F15.opPattern","COPY",EDGE,{"derivedFrom":makeQuery(id+"F4.opExtrude","CAP_EDGE",EDGE,{"disambiguationData":[OSD([sQuery(id+"F3.wireOp",EDGE,"E1.right")])],"isStart":false}),"instanceName":"1"});Q1=makeQuery(id+"F24.imprint","IMPRINT",FACE,{"disambiguationData":[TD([[makeQuery(id+"F24.imprint","IMPRINT",EDGE,{"derivedFrom":subQ1}),1.0]])]});}
            var Q2;
            {var subQ1=makeQuery(id+"F15.opPattern","COPY",EDGE,{"derivedFrom":makeQuery(id+"F4.opExtrude","CAP_EDGE",EDGE,{"disambiguationData":[OSD([sQuery(id+"F3.wireOp",EDGE,"E1.top")])],"isStart":false}),"instanceName":"1"});Q2=makeQuery(id+"F24.imprint","IMPRINT",FACE,{"disambiguationData":[TD([[makeQuery(id+"F24.imprint","IMPRINT",EDGE,{"derivedFrom":subQ1}),-1.0]])]});}
            var Q3;
            {var subQ4=makeQuery(id+"F15.opPattern","COPY",EDGE,{"derivedFrom":makeQuery(id+"F4.opExtrude","CAP_EDGE",EDGE,{"disambiguationData":[OSD([sQuery(id+"F3.wireOp",EDGE,"E1.top")])],"isStart":false}),"instanceName":"1"});Q3=makeQuery(id+"F24.imprint","IMPRINT",FACE,{"disambiguationData":[TD([[makeQuery(id+"F24.imprint","IMPRINT",EDGE,{"derivedFrom":subQ4}),1.0]])]});}
            extrude(context, id + "F25", {"entities" : qUnion([Q0, Q1, Q2, Q3]), "depth" : 38.1 * mm, "offsetDistance" : 25.4 * mm});
        }
    });
